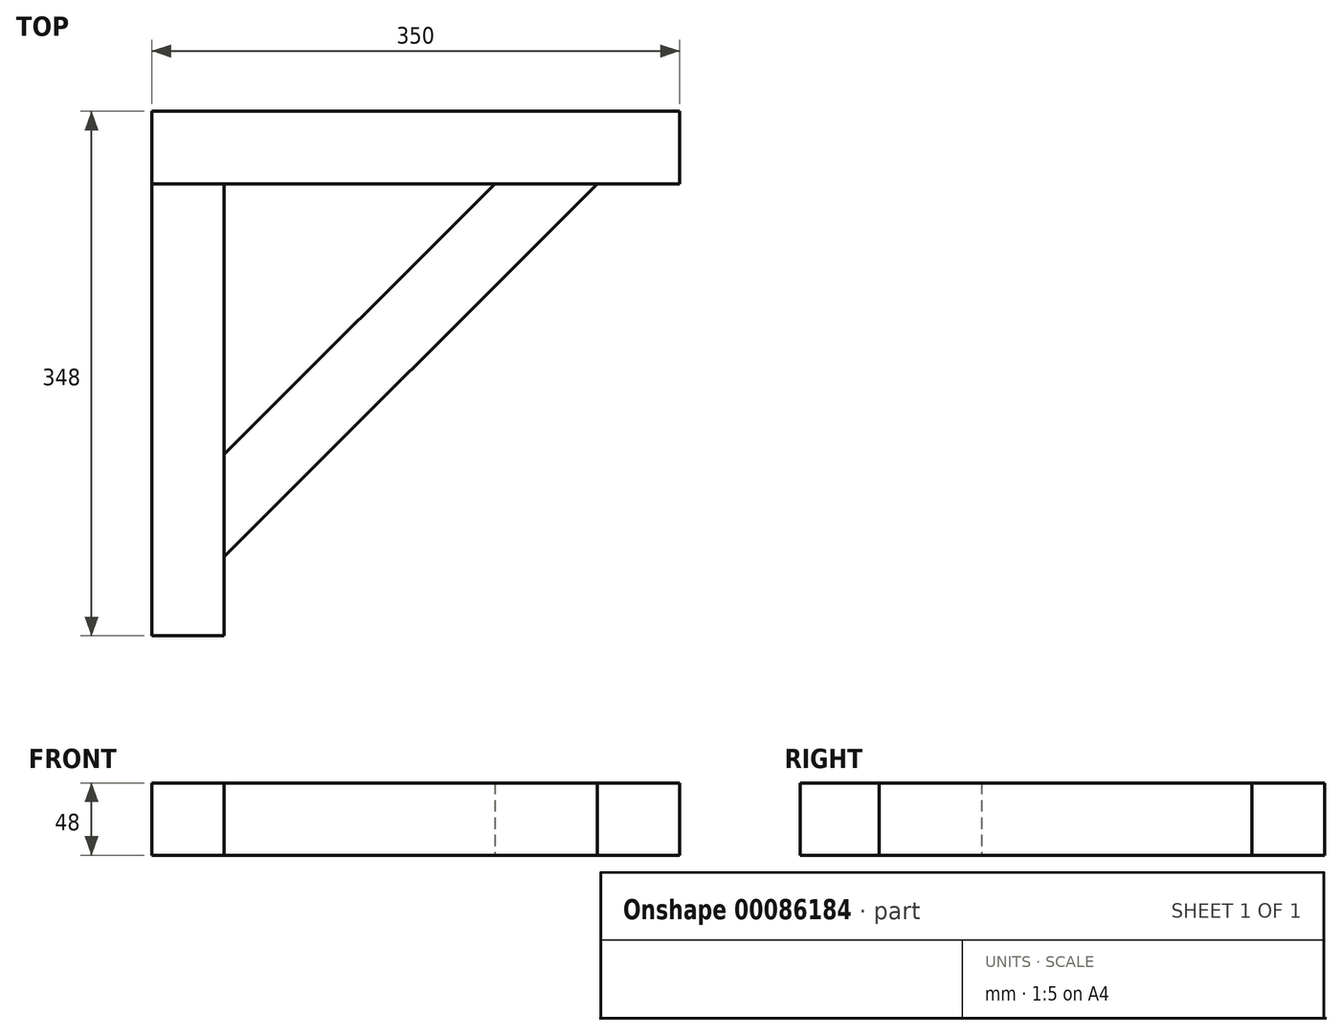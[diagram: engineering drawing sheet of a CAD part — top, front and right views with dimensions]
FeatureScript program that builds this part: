
annotation { "Feature Type Name" : "Feature", "Feature Type Description" : "" }
export const myFeature = defineFeature(function(context is Context, id is Id, definition is map)
    precondition{}
    {
        {
            assignVariable(context, id + "F0", {"name" : "T", "anyValue" : 48});
        }
        {
            var Q0;
            Q0=qCreatedBy(makeId("Top.planeOp"),FACE);
            var sketch = newSketch(context, id + "F1", { "sketchPlane" : qUnion([Q0])});
            skLineSegment(sketch, "E0.bottom", {"start": v(0, -48) * mm, "end": v(350, -48) * mm});
            skLineSegment(sketch, "E0.top", {"start": v(0, 0) * mm, "end": v(350, 0) * mm});
            skLineSegment(sketch, "E0.left", {"start": v(0, 0) * mm, "end": v(0, -48) * mm});
            skLineSegment(sketch, "E0.right", {"start": v(350, 0) * mm, "end": v(350, -48) * mm});
            skSolve(sketch);
        }
        {
            var Q0;
            Q0 = qSketchRegion(id + "F1", true);
            extrude(context, id + "F2", {"entities" : qUnion([Q0]), "depth" : (getVariable(context, 'T')) * mm});
        }
        {
            var Q0;
            Q0=qCreatedBy(makeId("Top.planeOp"),FACE);
            var sketch = newSketch(context, id + "F3", { "sketchPlane" : qUnion([Q0])});
            skLineSegment(sketch, "E1.bottom", {"start": v(48, -48) * mm, "end": v(0, -48) * mm});
            skLineSegment(sketch, "E1.top", {"start": v(48, -348) * mm, "end": v(0, -348) * mm});
            skLineSegment(sketch, "E1.left", {"start": v(48, -48) * mm, "end": v(48, -348) * mm});
            skLineSegment(sketch, "E1.right", {"start": v(0, -48) * mm, "end": v(0, -348) * mm});
            skSolve(sketch);
        }
        {
            var Q0;
            Q0 = qSketchRegion(id + "F3", true);
            extrude(context, id + "F4", {"entities" : qUnion([Q0]), "depth" : (getVariable(context, 'T')) * mm});
        }
        {
            var Q0;
            Q0=qCreatedBy(makeId("Top.planeOp"),FACE);
            var sketch = newSketch(context, id + "F5", { "sketchPlane" : qUnion([Q0])});
            skLineSegment(sketch, "E2", {"start": v(295.49, -48) * mm, "end": v(227.6, -48) * mm});
            skLineSegment(sketch, "E3", {"start": v(227.6, -48) * mm, "end": v(48, -227.6) * mm});
            skLineSegment(sketch, "E4", {"start": v(48, -227.6) * mm, "end": v(48, -295.49) * mm});
            skLineSegment(sketch, "E5", {"start": v(48, -295.49) * mm, "end": v(295.49, -48) * mm});
            skSolve(sketch);
        }
        {
            var Q0;
            Q0 = qSketchRegion(id + "F5", true);
            extrude(context, id + "F6", {"entities" : qUnion([Q0]), "depth" : (getVariable(context, 'T')) * mm});
        }
    });
